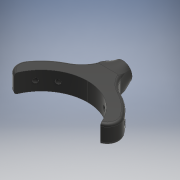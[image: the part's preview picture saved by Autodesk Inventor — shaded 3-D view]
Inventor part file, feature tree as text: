
AUTODESK INVENTOR PART (.ipt)
format: ipt  version: 2017 (Build 210142000, 142)  size: 425,984 bytes
history: native  units: mm
features: sketch x9, extrude x7, plane x7, fillet x4, loft x1, other x1, projected_geometry x1
ambient origin geometry x8: Origin, YZ Plane, XZ Plane, XY Plane, X Axis, Y Axis, Z Axis, Center Point
bodies: Solid1 (feature_tree)
feature tree (30):
  extrude  "Extrusion1"  Depth=35.0mm
  plane  "Work Plane1"
  sketch  "Sketch3"  dims[d3=10.0mm d7=6.981317mm]
  sketch  "Sketch4"  dims[d8=60.0deg d9=7.0mm d11=10.0mm d12=14.0mm]
  plane  "Work Plane2"
  extrude  "Extrusion2"  Depth=6.981317mm
  loft  "Loft1"
  fillet  "Fillet1"  Radius=10.0mm
  fillet  "Fillet2"  Radius=14.0mm
  extrude  "Extrusion3"  [1 undecoded]
  plane  "Work Plane3"
  sketch  "Sketch6"  dims[d16=-5.5mm d17=14.0mm d18=0.0mm]
  plane  "Work Plane4"
  plane  "Work Plane5"
  plane  "Work Plane6"
  plane  "Work Plane7"
  sketch  "Sketch7"  dims[d19=0.0mm d20=90.0deg d21=0.0mm d22=90.0deg]
  sketch  "Sketch8"  dims[d23=2.0mm d24=2.0mm]
  sketch  "Sketch9"  dims[d25=8.2mm d26=22.0mm d27=0.0mm d28=6.981317mm d29=60.0deg]
  sketch  "Sketch10"  dims[d30=120.0deg d31=24.43461mm d32=3.5mm d33=3.5mm d34=3.5mm d35=3.5mm d36=22.0mm d37=0.0mm d38=22.0mm d39=0.0mm d40=22.0mm d41=0.0mm d42=22.0mm d43=0.0mm d44=4.0mm d45=4.0mm]
  extrude  "Extrusion4"  Depth=14.0mm TaperAngle=0.0deg
  extrude  "Extrusion5"  TaperAngle=0.0deg  [1 undecoded]
  extrude  "Extrusion6"  Depth=2.0mm
  extrude  "Extrusion7"  Depth=22.0mm TaperAngle=0.0deg
  fillet  "Fillet3"  Radius=6.981317mm
  fillet  "Fillet4"  [1 undecoded]
  sketch  "Sketch1"  dims[d1=24.43461mm d2=35.0mm]
  other  "Edges1"
  sketch  "Sketch5"  dims[d13=14.0mm d14=0.0mm d15=-11.0mm]
  projected_geometry  "Project Cut Edges2"
note: 3 required parameter values undecoded (feature->parameter linkage not recoverable at this tier; creation-order binding heuristic only, values carry confidence <= 0.55)
